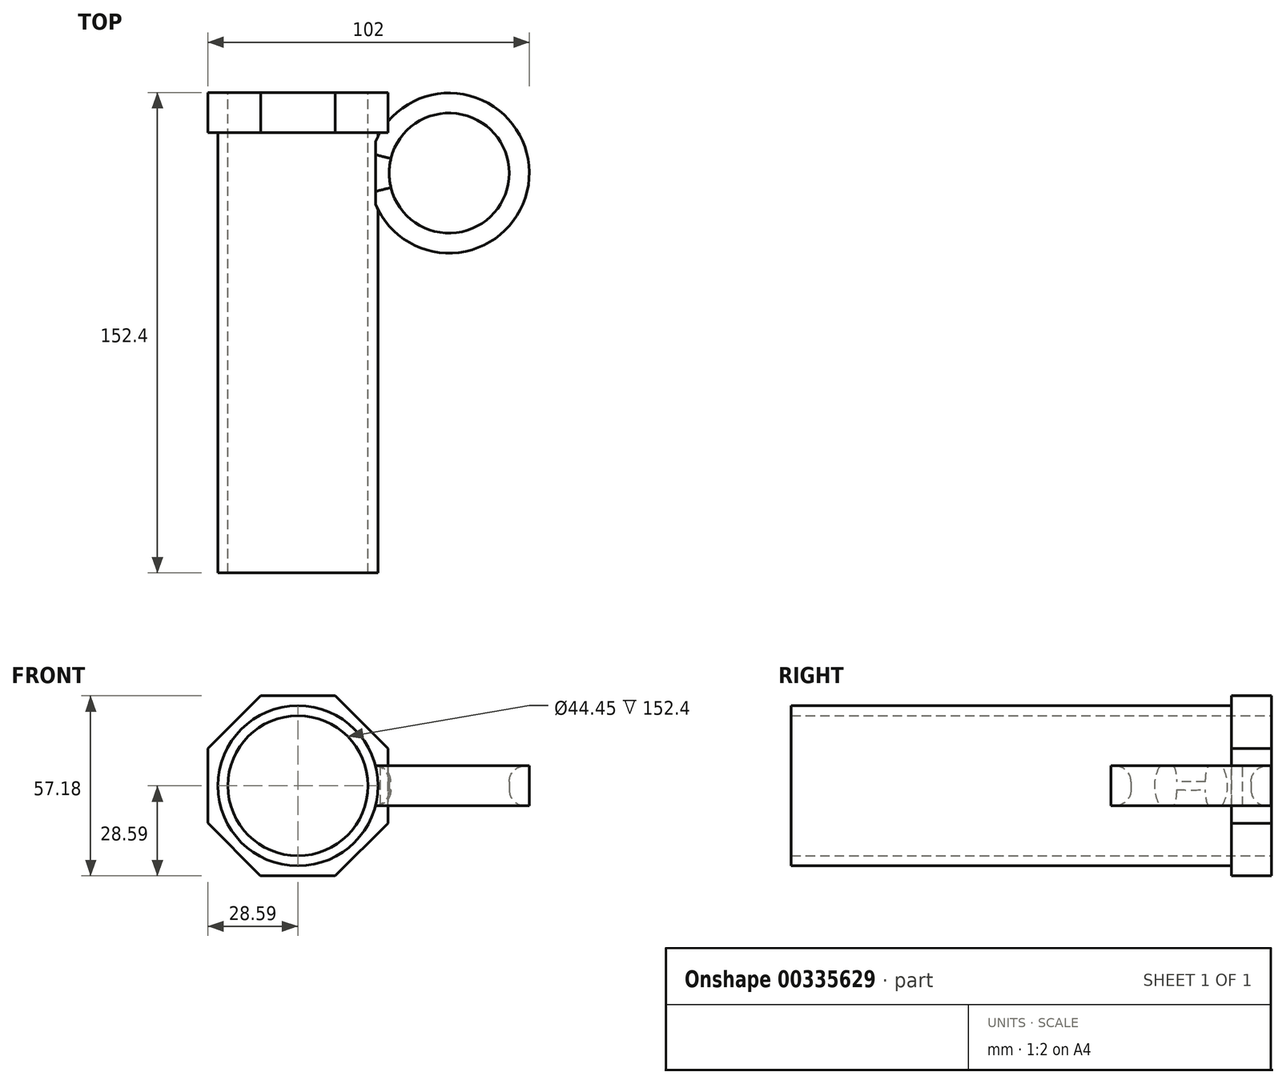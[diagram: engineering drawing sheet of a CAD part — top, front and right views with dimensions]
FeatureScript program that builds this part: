
annotation { "Feature Type Name" : "Feature", "Feature Type Description" : "" }
export const myFeature = defineFeature(function(context is Context, id is Id, definition is map)
    precondition{}
    {
        {
            var Q0;
            Q0=qCreatedBy(makeId("Front.planeOp"),FACE);
            var sketch = newSketch(context, id + "F0", { "sketchPlane" : qUnion([Q0])});
            skCircle(sketch, "E0.cCircle", {"center": v(0, 0) * mm, "radius": 28.57 * mm, "construction": true});
            skLineSegment(sketch, "E0.0", {"start": v(-28.56, 11.87) * mm, "end": v(-11.8, 28.59) * mm});
            skLineSegment(sketch, "E0.1", {"start": v(-11.8, 28.59) * mm, "end": v(11.87, 28.56) * mm});
            skLineSegment(sketch, "E0.2", {"start": v(11.87, 28.56) * mm, "end": v(28.59, 11.8) * mm});
            skLineSegment(sketch, "E0.3", {"start": v(28.59, 11.8) * mm, "end": v(28.56, -11.87) * mm});
            skLineSegment(sketch, "E0.4", {"start": v(28.56, -11.87) * mm, "end": v(11.8, -28.59) * mm});
            skLineSegment(sketch, "E0.5", {"start": v(11.8, -28.59) * mm, "end": v(-11.87, -28.56) * mm});
            skLineSegment(sketch, "E0.6", {"start": v(-11.87, -28.56) * mm, "end": v(-28.59, -11.8) * mm});
            skLineSegment(sketch, "E0.7", {"start": v(-28.59, -11.8) * mm, "end": v(-28.56, 11.87) * mm});
            skPoint(sketch, "E0.0.midPoint", {"position": v(-20.18, 20.23) * mm});
            skSolve(sketch);
        }
        {
            var Q0;
            Q0 = qSketchRegion(id + "F0", true);
            extrude(context, id + "F1", {"entities" : qUnion([Q0]), "depth" : 12.7 * mm});
        }
        {
            var Q0;
            Q0=makeQuery(id+"F1.opExtrude","CAP_FACE",FACE,{"disambiguationData":[OSD([sQuery(id+"F0.wireOp",EDGE,"E0.0"),sQuery(id+"F0.wireOp",EDGE,"E0.1"),sQuery(id+"F0.wireOp",EDGE,"E0.2"),sQuery(id+"F0.wireOp",EDGE,"E0.3"),sQuery(id+"F0.wireOp",EDGE,"E0.4"),sQuery(id+"F0.wireOp",EDGE,"E0.5"),sQuery(id+"F0.wireOp",EDGE,"E0.6"),sQuery(id+"F0.wireOp",EDGE,"E0.7")])],"isStart":false});
            var sketch = newSketch(context, id + "F2", { "sketchPlane" : qUnion([Q0])});
            skCircle(sketch, "E1", {"center": v(0, 0) * mm, "radius": 25.4 * mm});
            skSolve(sketch);
        }
        {
            var Q0;
            Q0 = qSketchRegion(id + "F2", true);
            extrude(context, id + "F3", {"entities" : qUnion([Q0]), "operationType" : NewBodyOperationType.ADD, "depth" : 139.7 * mm});
        }
        {
            var Q0;
            Q0=makeQuery(id+"F1.opExtrude","CAP_FACE",FACE,{"disambiguationData":[OSD([sQuery(id+"F0.wireOp",EDGE,"E0.0"),sQuery(id+"F0.wireOp",EDGE,"E0.1"),sQuery(id+"F0.wireOp",EDGE,"E0.2"),sQuery(id+"F0.wireOp",EDGE,"E0.3"),sQuery(id+"F0.wireOp",EDGE,"E0.4"),sQuery(id+"F0.wireOp",EDGE,"E0.5"),sQuery(id+"F0.wireOp",EDGE,"E0.6"),sQuery(id+"F0.wireOp",EDGE,"E0.7")])],"isStart":true});
            var sketch = newSketch(context, id + "F4", { "sketchPlane" : qUnion([Q0])});
            skCircle(sketch, "E2", {"center": v(0, 0) * mm, "radius": 22.23 * mm});
            skSolve(sketch);
        }
        {
            var Q0;
            Q0=sQuery(id+"F4.wireOp",VERTEX,"E2.center");
            var Q1;
            Q1=makeQuery(id+"F1.opExtrude","SWEPT_BODY",BODY,{"disambiguationData":[OSD([sQuery(id+"F0.wireOp",EDGE,"E0.0"),sQuery(id+"F0.wireOp",EDGE,"E0.1"),sQuery(id+"F0.wireOp",EDGE,"E0.2"),sQuery(id+"F0.wireOp",EDGE,"E0.3"),sQuery(id+"F0.wireOp",EDGE,"E0.4"),sQuery(id+"F0.wireOp",EDGE,"E0.5"),sQuery(id+"F0.wireOp",EDGE,"E0.6"),sQuery(id+"F0.wireOp",EDGE,"E0.7")])]});
            hole(context, id + "F5", {"style" : HoleStyle.SIMPLE, "endStyle" : HoleEndStyle.BLIND, "holeDiameter" : 44.45 * mm, "holeDepth" : 247.65 * mm, "tappedDepth" : 12.7 * mm, "tapClearance" : 3, "locations" : qUnion([Q0]), "scope" : qUnion([Q1])});
        }
        {
            var Q0;
            Q0=qCreatedBy(makeId("Top.planeOp"),FACE);
            var sketch = newSketch(context, id + "F6", { "sketchPlane" : qUnion([Q0])});
            skCircle(sketch, "E3", {"center": v(48, -25.53) * mm, "radius": 25.4 * mm});
            skCircle(sketch, "E4", {"center": v(48, -25.53) * mm, "radius": 19.05 * mm});
            skCircle(sketch, "E5.MirrorC", {"center": v(-48, -25.53) * mm, "radius": 25.4 * mm});
            skCircle(sketch, "E6.MirrorC", {"center": v(-48, -25.53) * mm, "radius": 19.05 * mm});
            skSolve(sketch);
        }
        {
            var Q0;
            Q0=makeQuery(id+"F6.imprint","IMPRINT",FACE,{"disambiguationData":[TD([[makeQuery(id+"F6.imprint","IMPRINT",EDGE,{"derivedFrom":sQuery(id+"F6.wireOp",EDGE,"E3")}),1.0]])]});
            var Q1;
            Q1=makeQuery(id+"F6.imprint","IMPRINT",FACE,{"disambiguationData":[TD([[makeQuery(id+"F6.imprint","IMPRINT",EDGE,{"derivedFrom":sQuery(id+"F6.wireOp",EDGE,"E5.MirrorC")}),-1.0]])]});
            extrude(context, id + "F7", {"entities" : qUnion([Q0, Q1]), "operationType" : NewBodyOperationType.ADD, "depth" : 6.35 * mm, "hasSecondDirection" : true, "secondDirectionOppositeDirection" : true, "secondDirectionDepth" : 6.35 * mm});
        }
        {
            var Q0;
            Q0=makeQuery(id+"F7.opExtrude","CAP_EDGE",EDGE,{"disambiguationData":[OSD([sQuery(id+"F6.wireOp",EDGE,"E6.MirrorC")])],"isStart":false});
            var Q1;
            Q1=makeQuery(id+"F7.opExtrude","CAP_EDGE",EDGE,{"disambiguationData":[OSD([sQuery(id+"F6.wireOp",EDGE,"E4")])],"isStart":false});
            var Q2;
            Q2=makeQuery(id+"F7.opExtrude","CAP_EDGE",EDGE,{"disambiguationData":[OSD([sQuery(id+"F6.wireOp",EDGE,"E6.MirrorC")])],"isStart":true});
            var Q3;
            Q3=makeQuery(id+"F7.opExtrude","CAP_EDGE",EDGE,{"disambiguationData":[OSD([sQuery(id+"F6.wireOp",EDGE,"E4")])],"isStart":true});
            fillet(context, id + "F8", {"entities" : qUnion([Q0, Q1, Q2, Q3]), "radius" : 5.08 * mm, "tangentPropagation" : true, "allowEdgeOverflow" : false});
        }
    });
